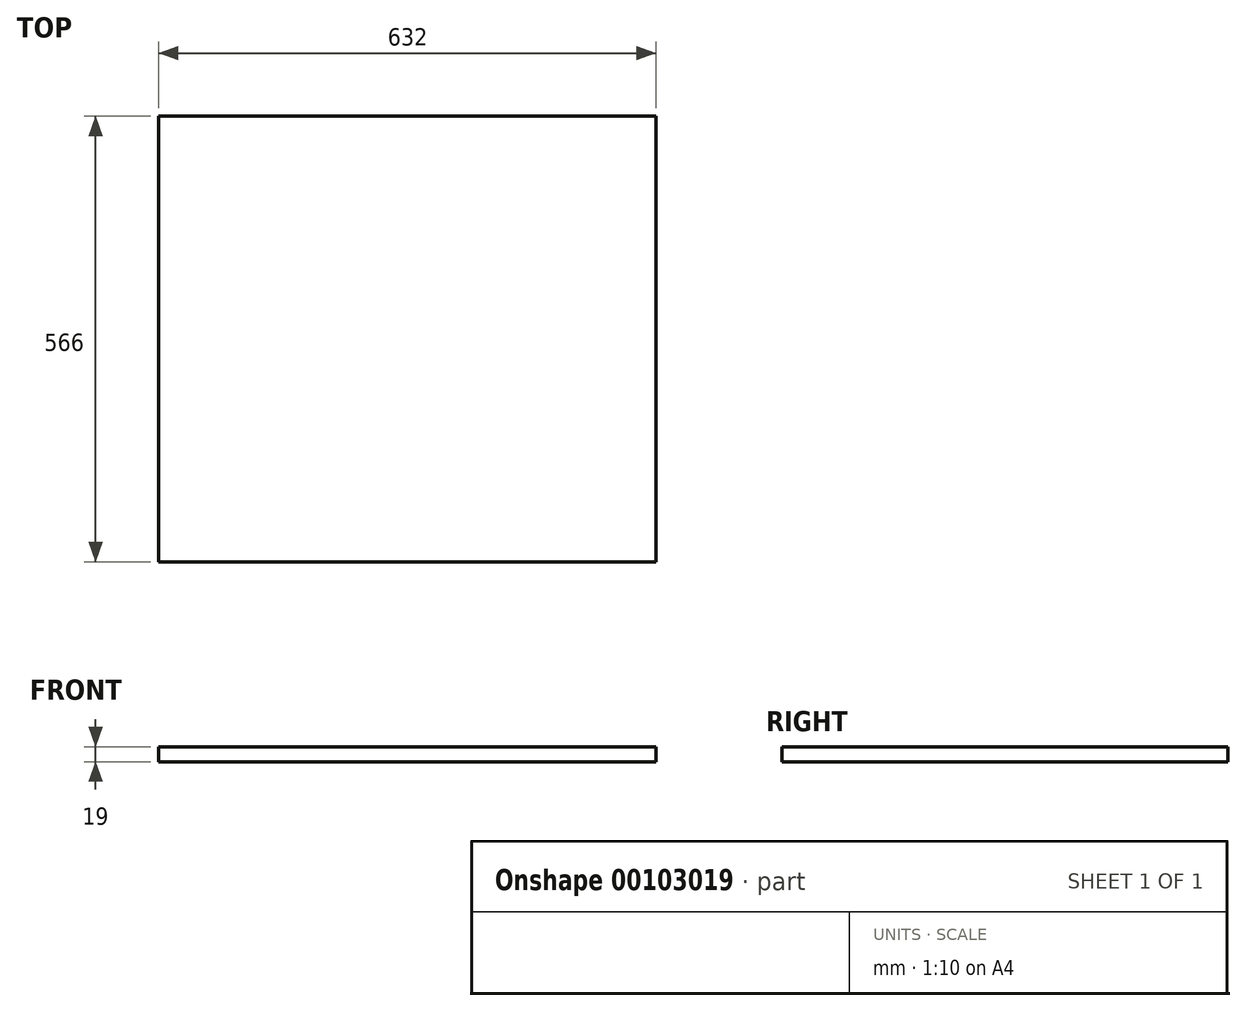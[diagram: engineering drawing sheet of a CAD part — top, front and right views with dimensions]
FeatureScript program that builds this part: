
annotation { "Feature Type Name" : "Feature", "Feature Type Description" : "" }
export const myFeature = defineFeature(function(context is Context, id is Id, definition is map)
    precondition{}
    {
        {
            var Q0;
            Q0=qCreatedBy(makeId("Top.planeOp"),FACE);
            var sketch = newSketch(context, id + "F0", { "sketchPlane" : qUnion([Q0])});
            skLineSegment(sketch, "E0.bottom", {"start": v(-70.96, 65.05) * mm, "end": v(561.04, 65.05) * mm});
            skLineSegment(sketch, "E0.top", {"start": v(-70.96, -500.95) * mm, "end": v(561.04, -500.95) * mm});
            skLineSegment(sketch, "E0.left", {"start": v(-70.96, 65.05) * mm, "end": v(-70.96, -500.95) * mm});
            skLineSegment(sketch, "E0.right", {"start": v(561.04, 65.05) * mm, "end": v(561.04, -500.95) * mm});
            skSolve(sketch);
        }
        {
            var Q0;
            Q0=qSketchRegion(id+"F0",true);
            extrude(context, id + "F1", {"entities" : qUnion([Q0]), "depth" : 19 * mm});
        }
    });
